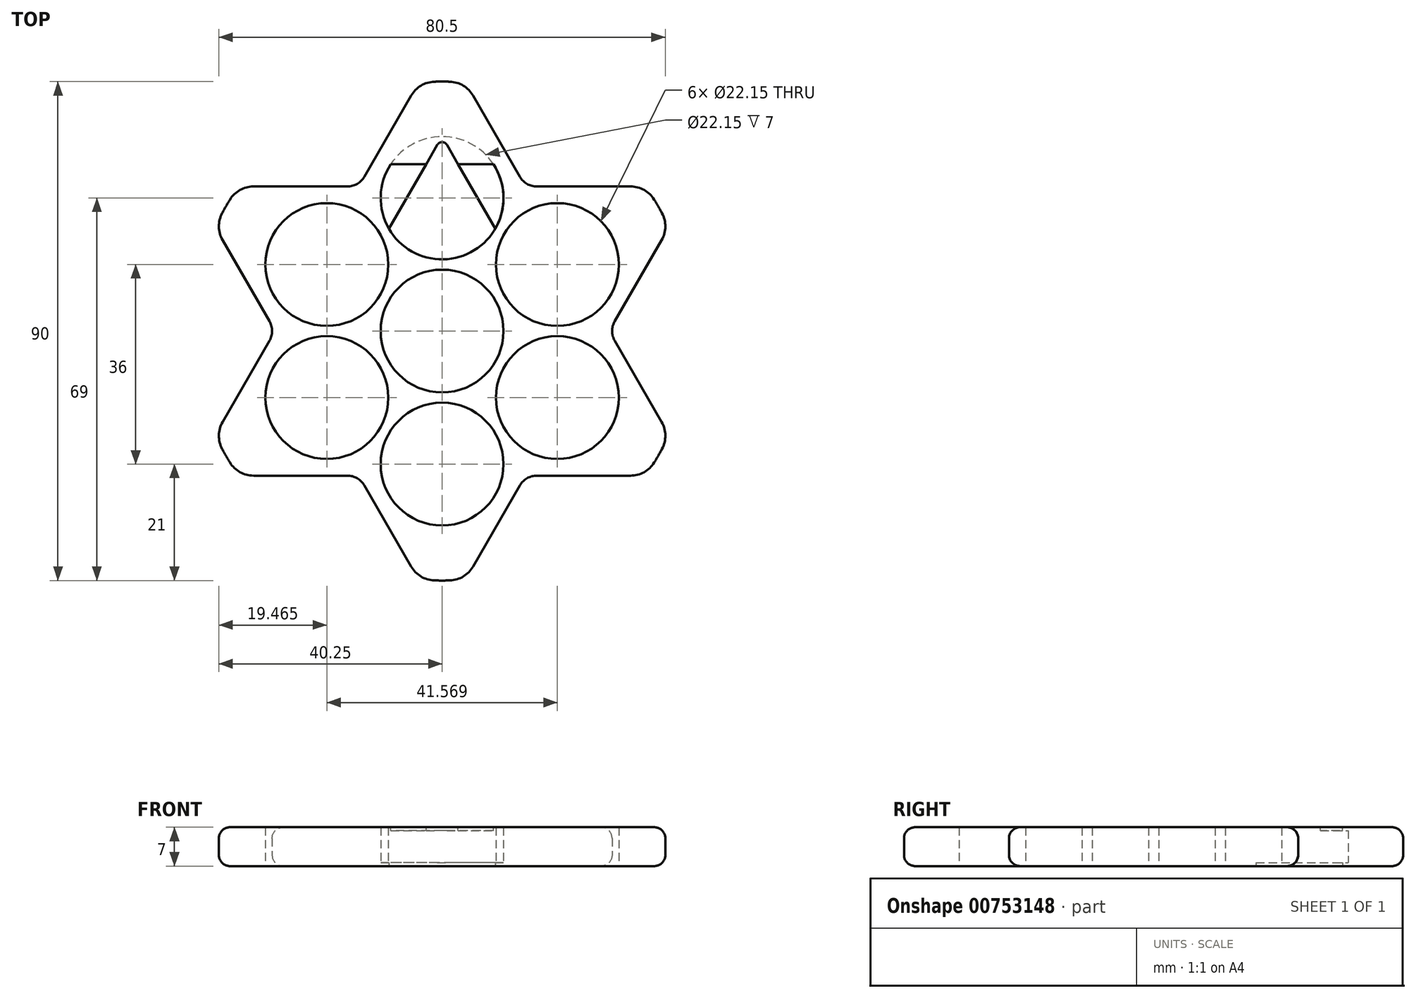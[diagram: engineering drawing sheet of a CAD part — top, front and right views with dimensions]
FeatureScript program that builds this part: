
annotation { "Feature Type Name" : "Feature", "Feature Type Description" : "" }
export const myFeature = defineFeature(function(context is Context, id is Id, definition is map)
    precondition{}
    {
        {
            var Q0;
            Q0=qCreatedBy(makeId("Top.planeOp"),FACE);
            var sketch = newSketch(context, id + "F0", { "sketchPlane" : qUnion([Q0])});
            skCircle(sketch, "E0", {"center": v(0, 0) * mm, "radius": 11.07 * mm});
            skLineSegment(sketch, "E1", {"start": v(-34, -26.08) * mm, "end": v(-17.08, -26.08) * mm});
            skLineSegment(sketch, "E2", {"start": v(39.58, 16.4) * mm, "end": v(31.12, 1.75) * mm});
            skCircle(sketch, "E3", {"center": v(-20.78, 12) * mm, "radius": 11.07 * mm});
            skLineSegment(sketch, "E4.trimOffspring", {"start": v(-31.12, -1.75) * mm, "end": v(-39.58, -16.4) * mm});
            skLineSegment(sketch, "E5.trimOffspring", {"start": v(14.04, 27.83) * mm, "end": v(5.58, 42.48) * mm});
            skLineSegment(sketch, "E6.trimOffspring", {"start": v(17.08, -26.08) * mm, "end": v(34, -26.08) * mm});
            skLineSegment(sketch, "E7", {"start": v(-45.16, 26.08) * mm, "end": v(45.16, -26.08) * mm, "construction": true});
            skLineSegment(sketch, "E8", {"start": v(45.16, 26.08) * mm, "end": v(-45.16, -26.08) * mm, "construction": true});
            skLineSegment(sketch, "E9", {"start": v(0, -52.15) * mm, "end": v(0, 52.15) * mm, "construction": true});
            skLineSegment(sketch, "E10.trimOffspring", {"start": v(-31.12, 1.75) * mm, "end": v(-39.58, 16.4) * mm});
            skLineSegment(sketch, "E11.trimOffspring", {"start": v(14.04, -27.83) * mm, "end": v(5.58, -42.48) * mm});
            skLineSegment(sketch, "E12.trimOffspring", {"start": v(17.08, 26.08) * mm, "end": v(34, 26.07) * mm});
            skArc(sketch, "E13", {"start": v(1.4, 44.98) * mm, "mid": v(0, 45) * mm, "end": v(-1.4, 44.98) * mm});
            skLineSegment(sketch, "E14.trimOffspring", {"start": v(-5.58, 42.48) * mm, "end": v(-14.04, 27.83) * mm});
            skArc(sketch, "E15.trimOffspring", {"start": v(39.66, 21.27) * mm, "mid": v(38.97, 22.5) * mm, "end": v(38.25, 23.7) * mm});
            skArc(sketch, "E16.trimOffspring", {"start": v(-38.25, 23.7) * mm, "mid": v(-38.97, 22.5) * mm, "end": v(-39.66, 21.27) * mm});
            skLineSegment(sketch, "E17.trimOffspring", {"start": v(-34, 26.08) * mm, "end": v(-17.08, 26.07) * mm});
            skArc(sketch, "E18.trimOffspring", {"start": v(-39.66, -21.27) * mm, "mid": v(-38.97, -22.5) * mm, "end": v(-38.25, -23.7) * mm});
            skLineSegment(sketch, "E19.trimOffspring", {"start": v(-5.58, -42.48) * mm, "end": v(-14.04, -27.83) * mm});
            skArc(sketch, "E20.trimOffspring", {"start": v(38.25, -23.7) * mm, "mid": v(38.97, -22.5) * mm, "end": v(39.66, -21.27) * mm});
            skArc(sketch, "E21.trimOffspring", {"start": v(-1.4, -44.98) * mm, "mid": v(0, -45) * mm, "end": v(1.4, -44.98) * mm});
            skLineSegment(sketch, "E22.trimOffspring", {"start": v(39.58, -16.4) * mm, "end": v(31.12, -1.75) * mm});
            skPoint(sketch, "E23.visualSharp", {"position": v(-4.24, 44.8) * mm});
            skArc(sketch, "E23.filletArc", {"start": v(-1.4, 44.98) * mm, "mid": v(-3.82, 44.27) * mm, "end": v(-5.58, 42.48) * mm});
            skPoint(sketch, "E24.visualSharp", {"position": v(4.24, 44.8) * mm});
            skArc(sketch, "E24.filletArc", {"start": v(5.58, 42.48) * mm, "mid": v(3.82, 44.27) * mm, "end": v(1.4, 44.98) * mm});
            skPoint(sketch, "E25.visualSharp", {"position": v(15.05, 26.08) * mm});
            skArc(sketch, "E25.filletArc", {"start": v(14.04, 27.83) * mm, "mid": v(15.33, 26.54) * mm, "end": v(17.08, 26.08) * mm});
            skPoint(sketch, "E26.visualSharp", {"position": v(36.68, 26.07) * mm});
            skArc(sketch, "E26.filletArc", {"start": v(38.25, 23.7) * mm, "mid": v(36.43, 25.44) * mm, "end": v(34, 26.07) * mm});
            skPoint(sketch, "E27.visualSharp", {"position": v(40.92, 18.72) * mm});
            skArc(sketch, "E27.filletArc", {"start": v(39.58, 16.4) * mm, "mid": v(40.25, 18.83) * mm, "end": v(39.66, 21.27) * mm});
            skPoint(sketch, "E28.visualSharp", {"position": v(30.1, 0) * mm});
            skArc(sketch, "E28.filletArc", {"start": v(31.12, 1.75) * mm, "mid": v(30.65, 0) * mm, "end": v(31.12, -1.75) * mm});
            skPoint(sketch, "E29.visualSharp", {"position": v(40.92, -18.72) * mm});
            skArc(sketch, "E29.filletArc", {"start": v(39.66, -21.27) * mm, "mid": v(40.25, -18.83) * mm, "end": v(39.58, -16.4) * mm});
            skPoint(sketch, "E30.visualSharp", {"position": v(36.68, -26.08) * mm});
            skArc(sketch, "E30.filletArc", {"start": v(34, -26.07) * mm, "mid": v(36.43, -25.44) * mm, "end": v(38.25, -23.7) * mm});
            skPoint(sketch, "E31.visualSharp", {"position": v(15.05, -26.08) * mm});
            skArc(sketch, "E31.filletArc", {"start": v(17.08, -26.07) * mm, "mid": v(15.33, -26.54) * mm, "end": v(14.04, -27.82) * mm});
            skPoint(sketch, "E32.visualSharp", {"position": v(4.24, -44.8) * mm});
            skArc(sketch, "E32.filletArc", {"start": v(1.4, -44.98) * mm, "mid": v(3.82, -44.27) * mm, "end": v(5.58, -42.48) * mm});
            skPoint(sketch, "E33.visualSharp", {"position": v(-4.24, -44.8) * mm});
            skArc(sketch, "E33.filletArc", {"start": v(-5.58, -42.48) * mm, "mid": v(-3.82, -44.27) * mm, "end": v(-1.4, -44.98) * mm});
            skPoint(sketch, "E34.visualSharp", {"position": v(-15.05, -26.08) * mm});
            skArc(sketch, "E34.filletArc", {"start": v(-14.04, -27.83) * mm, "mid": v(-15.33, -26.54) * mm, "end": v(-17.08, -26.07) * mm});
            skPoint(sketch, "E35.visualSharp", {"position": v(-36.68, -26.08) * mm});
            skArc(sketch, "E35.filletArc", {"start": v(-38.25, -23.7) * mm, "mid": v(-36.43, -25.44) * mm, "end": v(-34, -26.08) * mm});
            skPoint(sketch, "E36.visualSharp", {"position": v(-40.92, -18.72) * mm});
            skArc(sketch, "E36.filletArc", {"start": v(-39.58, -16.4) * mm, "mid": v(-40.25, -18.83) * mm, "end": v(-39.66, -21.27) * mm});
            skPoint(sketch, "E37.visualSharp", {"position": v(-30.1, 0) * mm});
            skArc(sketch, "E37.filletArc", {"start": v(-31.12, -1.75) * mm, "mid": v(-30.65, 0) * mm, "end": v(-31.12, 1.75) * mm});
            skPoint(sketch, "E38.visualSharp", {"position": v(-40.92, 18.72) * mm});
            skArc(sketch, "E38.filletArc", {"start": v(-39.66, 21.27) * mm, "mid": v(-40.25, 18.83) * mm, "end": v(-39.58, 16.4) * mm});
            skPoint(sketch, "E39.visualSharp", {"position": v(-36.68, 26.08) * mm});
            skArc(sketch, "E39.filletArc", {"start": v(-34, 26.07) * mm, "mid": v(-36.43, 25.44) * mm, "end": v(-38.25, 23.7) * mm});
            skPoint(sketch, "E40.visualSharp", {"position": v(-15.05, 26.07) * mm});
            skArc(sketch, "E40.filletArc", {"start": v(-17.08, 26.07) * mm, "mid": v(-15.33, 26.54) * mm, "end": v(-14.04, 27.83) * mm});
            skPoint(sketch, "E41", {"position": v(0, 45) * mm});
            skPoint(sketch, "E42", {"position": v(-38.97, 22.5) * mm});
            skPoint(sketch, "E43", {"position": v(38.97, 22.5) * mm});
            skPoint(sketch, "E44", {"position": v(38.97, -22.5) * mm});
            skPoint(sketch, "E45", {"position": v(0, -45) * mm});
            skPoint(sketch, "E46", {"position": v(-38.97, -22.5) * mm});
            skLineSegment(sketch, "E47", {"start": v(-34.15, 0) * mm, "end": v(34.15, 0) * mm, "construction": true});
            skLineSegment(sketch, "E48", {"start": v(-17.08, -29.57) * mm, "end": v(17.08, 29.58) * mm, "construction": true});
            skLineSegment(sketch, "E49", {"start": v(17.08, -29.57) * mm, "end": v(-17.08, 29.57) * mm, "construction": true});
            skCircle(sketch, "E50.1.0", {"center": v(-20.78, -12) * mm, "radius": 11.07 * mm});
            skCircle(sketch, "E50.2.0", {"center": v(0, -24) * mm, "radius": 11.07 * mm});
            skCircle(sketch, "E51.1.3.0", {"center": v(20.78, -12) * mm, "radius": 11.07 * mm});
            skCircle(sketch, "E51.1.4.0", {"center": v(20.78, 12) * mm, "radius": 11.07 * mm});
            skCircle(sketch, "E51.1.5.0", {"center": v(0, 24) * mm, "radius": 11.07 * mm});
            skSolve(sketch);
        }
        {
            var Q0;
            Q0=qSketchRegion(id+"F0",true);
            extrude(context, id + "F1", {"entities" : qUnion([Q0]), "depth" : 7 * mm, "offsetDistance" : 25 * mm});
        }
        {
            var Q0;
            Q0=makeQuery(id+"F1.opExtrude","CAP_FACE",FACE,{"disambiguationData":[OSD([sQuery(id+"F0.wireOp",EDGE,"E0"),sQuery(id+"F0.wireOp",EDGE,"E1"),sQuery(id+"F0.wireOp",EDGE,"E2"),sQuery(id+"F0.wireOp",EDGE,"E3"),sQuery(id+"F0.wireOp",EDGE,"E4.trimOffspring"),sQuery(id+"F0.wireOp",EDGE,"E5.trimOffspring"),sQuery(id+"F0.wireOp",EDGE,"E6.trimOffspring"),sQuery(id+"F0.wireOp",EDGE,"E10.trimOffspring"),sQuery(id+"F0.wireOp",EDGE,"E11.trimOffspring"),sQuery(id+"F0.wireOp",EDGE,"E12.trimOffspring"),sQuery(id+"F0.wireOp",EDGE,"E13"),sQuery(id+"F0.wireOp",EDGE,"E14.trimOffspring"),sQuery(id+"F0.wireOp",EDGE,"E15.trimOffspring"),sQuery(id+"F0.wireOp",EDGE,"E16.trimOffspring"),sQuery(id+"F0.wireOp",EDGE,"E17.trimOffspring"),sQuery(id+"F0.wireOp",EDGE,"E18.trimOffspring"),sQuery(id+"F0.wireOp",EDGE,"E19.trimOffspring"),sQuery(id+"F0.wireOp",EDGE,"E20.trimOffspring"),sQuery(id+"F0.wireOp",EDGE,"E21.trimOffspring"),sQuery(id+"F0.wireOp",EDGE,"E22.trimOffspring"),sQuery(id+"F0.wireOp",EDGE,"E23.filletArc"),sQuery(id+"F0.wireOp",EDGE,"E24.filletArc"),sQuery(id+"F0.wireOp",EDGE,"E25.filletArc"),sQuery(id+"F0.wireOp",EDGE,"E26.filletArc"),sQuery(id+"F0.wireOp",EDGE,"E27.filletArc"),sQuery(id+"F0.wireOp",EDGE,"E28.filletArc"),sQuery(id+"F0.wireOp",EDGE,"E29.filletArc"),sQuery(id+"F0.wireOp",EDGE,"E30.filletArc"),sQuery(id+"F0.wireOp",EDGE,"E31.filletArc"),sQuery(id+"F0.wireOp",EDGE,"E32.filletArc"),sQuery(id+"F0.wireOp",EDGE,"E33.filletArc"),sQuery(id+"F0.wireOp",EDGE,"E34.filletArc"),sQuery(id+"F0.wireOp",EDGE,"E35.filletArc"),sQuery(id+"F0.wireOp",EDGE,"E36.filletArc"),sQuery(id+"F0.wireOp",EDGE,"E37.filletArc"),sQuery(id+"F0.wireOp",EDGE,"E38.filletArc"),sQuery(id+"F0.wireOp",EDGE,"E39.filletArc"),sQuery(id+"F0.wireOp",EDGE,"E40.filletArc"),sQuery(id+"F0.wireOp",EDGE,"E50.1.0"),sQuery(id+"F0.wireOp",EDGE,"E50.2.0"),sQuery(id+"F0.wireOp",EDGE,"E51.1.3.0"),sQuery(id+"F0.wireOp",EDGE,"E51.1.4.0"),sQuery(id+"F0.wireOp",EDGE,"E51.1.5.0")])],"isStart":true});
            var sketch = newSketch(context, id + "F2", { "sketchPlane" : qUnion([Q0])});
            skLineSegment(sketch, "E52", {"start": v(-9.6, -18.46) * mm, "end": v(9.6, -18.46) * mm, "construction": true});
            skLineSegment(sketch, "E53", {"start": v(9.6, -18.46) * mm, "end": v(0.87, -33.58) * mm});
            skLineSegment(sketch, "E54", {"start": v(-0.87, -33.58) * mm, "end": v(-9.6, -18.46) * mm});
            skPoint(sketch, "E55.visualSharp", {"position": v(0, -35.08) * mm});
            skArc(sketch, "E55.filletArc", {"start": v(-0.87, -33.58) * mm, "mid": v(0, -34.08) * mm, "end": v(0.87, -33.58) * mm});
            skArc(sketch, "E56", {"start": v(-9.6, -18.46) * mm, "mid": v(0, -35.08) * mm, "end": v(9.6, -18.46) * mm});
            skSolve(sketch);
        }
        {
            var Q0;
            Q0 = qSketchRegion(id + "F2", true);
            extrude(context, id + "F3", {"entities" : qUnion([Q0]), "operationType" : NewBodyOperationType.ADD, "oppositeDirection" : true, "depth" : 0.6 * mm, "offsetDistance" : 25 * mm});
        }
        {
            var Q0;
            Q0=makeQuery(id+"F1.opExtrude","CAP_FACE",FACE,{"disambiguationData":[OSD([sQuery(id+"F0.wireOp",EDGE,"E0"),sQuery(id+"F0.wireOp",EDGE,"E1"),sQuery(id+"F0.wireOp",EDGE,"E2"),sQuery(id+"F0.wireOp",EDGE,"E3"),sQuery(id+"F0.wireOp",EDGE,"E4.trimOffspring"),sQuery(id+"F0.wireOp",EDGE,"E5.trimOffspring"),sQuery(id+"F0.wireOp",EDGE,"E6.trimOffspring"),sQuery(id+"F0.wireOp",EDGE,"E10.trimOffspring"),sQuery(id+"F0.wireOp",EDGE,"E11.trimOffspring"),sQuery(id+"F0.wireOp",EDGE,"E12.trimOffspring"),sQuery(id+"F0.wireOp",EDGE,"E13"),sQuery(id+"F0.wireOp",EDGE,"E14.trimOffspring"),sQuery(id+"F0.wireOp",EDGE,"E15.trimOffspring"),sQuery(id+"F0.wireOp",EDGE,"E16.trimOffspring"),sQuery(id+"F0.wireOp",EDGE,"E17.trimOffspring"),sQuery(id+"F0.wireOp",EDGE,"E18.trimOffspring"),sQuery(id+"F0.wireOp",EDGE,"E19.trimOffspring"),sQuery(id+"F0.wireOp",EDGE,"E20.trimOffspring"),sQuery(id+"F0.wireOp",EDGE,"E21.trimOffspring"),sQuery(id+"F0.wireOp",EDGE,"E22.trimOffspring"),sQuery(id+"F0.wireOp",EDGE,"E23.filletArc"),sQuery(id+"F0.wireOp",EDGE,"E24.filletArc"),sQuery(id+"F0.wireOp",EDGE,"E25.filletArc"),sQuery(id+"F0.wireOp",EDGE,"E26.filletArc"),sQuery(id+"F0.wireOp",EDGE,"E27.filletArc"),sQuery(id+"F0.wireOp",EDGE,"E28.filletArc"),sQuery(id+"F0.wireOp",EDGE,"E29.filletArc"),sQuery(id+"F0.wireOp",EDGE,"E30.filletArc"),sQuery(id+"F0.wireOp",EDGE,"E31.filletArc"),sQuery(id+"F0.wireOp",EDGE,"E32.filletArc"),sQuery(id+"F0.wireOp",EDGE,"E33.filletArc"),sQuery(id+"F0.wireOp",EDGE,"E34.filletArc"),sQuery(id+"F0.wireOp",EDGE,"E35.filletArc"),sQuery(id+"F0.wireOp",EDGE,"E36.filletArc"),sQuery(id+"F0.wireOp",EDGE,"E37.filletArc"),sQuery(id+"F0.wireOp",EDGE,"E38.filletArc"),sQuery(id+"F0.wireOp",EDGE,"E39.filletArc"),sQuery(id+"F0.wireOp",EDGE,"E40.filletArc"),sQuery(id+"F0.wireOp",EDGE,"E50.1.0"),sQuery(id+"F0.wireOp",EDGE,"E50.2.0"),sQuery(id+"F0.wireOp",EDGE,"E51.1.3.0"),sQuery(id+"F0.wireOp",EDGE,"E51.1.4.0"),sQuery(id+"F0.wireOp",EDGE,"E51.1.5.0")])],"isStart":false});
            var sketch = newSketch(context, id + "F4", { "sketchPlane" : qUnion([Q0])});
            skLineSegment(sketch, "E57", {"start": v(0, 12.93) * mm, "end": v(0, 12.93) * mm});
            skLineSegment(sketch, "E58", {"start": v(-2.89, 30.08) * mm, "end": v(-0.87, 33.58) * mm});
            skLineSegment(sketch, "E59", {"start": v(0.87, 33.58) * mm, "end": v(2.89, 30.08) * mm});
            skLineSegment(sketch, "E60", {"start": v(2.89, 30.08) * mm, "end": v(9.26, 30.08) * mm});
            skLineSegment(sketch, "E61", {"start": v(-9.26, 30.08) * mm, "end": v(-2.89, 30.08) * mm});
            skPoint(sketch, "E62.visualSharp", {"position": v(0, 35.08) * mm});
            skArc(sketch, "E62.filletArc", {"start": v(0.87, 33.58) * mm, "mid": v(0, 34.08) * mm, "end": v(-0.87, 33.58) * mm});
            skArc(sketch, "E63", {"start": v(9.26, 30.07) * mm, "mid": v(0, 35.08) * mm, "end": v(-9.26, 30.08) * mm});
            skSolve(sketch);
        }
        {
            var Q0;
            Q0 = qSketchRegion(id + "F4", true);
            extrude(context, id + "F5", {"entities" : qUnion([Q0]), "operationType" : NewBodyOperationType.ADD, "oppositeDirection" : true, "depth" : 0.6 * mm, "offsetDistance" : 25 * mm});
        }
        {
            var Q0;
            Q0=makeQuery(id+"F1.opExtrude","CAP_EDGE",EDGE,{"disambiguationData":[OSD([sQuery(id+"F0.wireOp",EDGE,"E1")])],"isStart":false});
            var Q1;
            Q1=makeQuery(id+"F1.opExtrude","CAP_EDGE",EDGE,{"disambiguationData":[OSD([sQuery(id+"F0.wireOp",EDGE,"E1")])],"isStart":true});
            fillet(context, id + "F6", {"entities" : qUnion([Q0, Q1]), "radius" : 2 * mm, "tangentPropagation" : true, "allowEdgeOverflow" : false});
        }
    });
